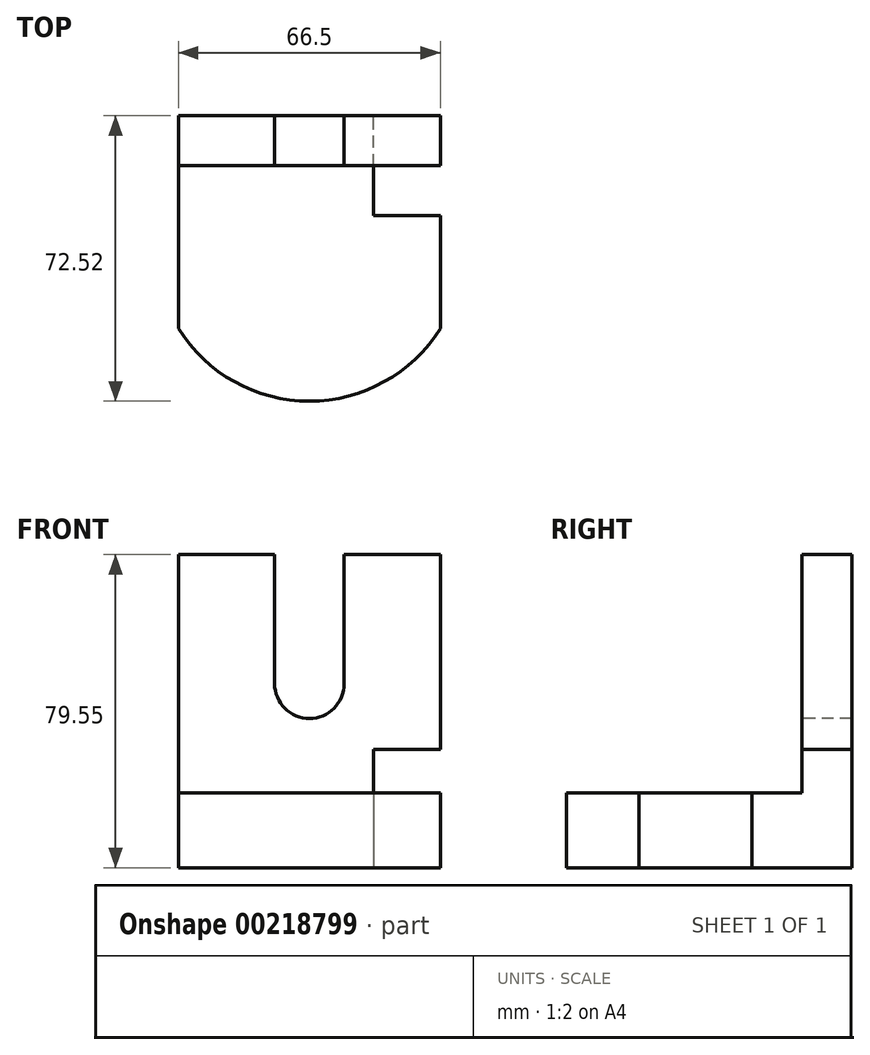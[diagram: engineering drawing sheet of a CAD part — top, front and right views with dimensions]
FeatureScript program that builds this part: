
annotation { "Feature Type Name" : "Feature", "Feature Type Description" : "" }
export const myFeature = defineFeature(function(context is Context, id is Id, definition is map)
    precondition{}
    {
        {
            var Q0;
            Q0=qCreatedBy(makeId("Top.planeOp"),FACE);
            var sketch = newSketch(context, id + "F0", { "sketchPlane" : qUnion([Q0])});
            skLineSegment(sketch, "E0.bottom", {"start": v(33.25, 20.67) * mm, "end": v(-33.25, 20.67) * mm});
            skLineSegment(sketch, "E0.left", {"start": v(33.25, 20.67) * mm, "end": v(33.25, -20.67) * mm});
            skLineSegment(sketch, "E0.right", {"start": v(-33.25, 20.67) * mm, "end": v(-33.25, -20.67) * mm});
            skPoint(sketch, "E0.middle", {"position": v(0, 0) * mm});
            skArc(sketch, "E1", {"start": v(-33.25, -20.67) * mm, "mid": v(0, -39.15) * mm, "end": v(33.25, -20.67) * mm});
            skSolve(sketch);
        }
        {
            var Q0;
            Q0=makeQuery(id+"F0.imprint","IMPRINT",FACE,{"disambiguationData":[TD([[makeQuery(id+"F0.imprint","IMPRINT",EDGE,{"derivedFrom":sQuery(id+"F0.wireOp",EDGE,"E0.bottom")}),1.0]])]});
            extrude(context, id + "F1", {"entities" : qUnion([Q0]), "depth" : 19.05 * mm});
        }
        {
            var Q0;
            Q0=makeQuery(id+"F1.opExtrude","SWEPT_FACE",FACE,{"disambiguationData":[OSD([sQuery(id+"F0.wireOp",EDGE,"E0.bottom")])]});
            var sketch = newSketch(context, id + "F2", { "sketchPlane" : qUnion([Q0])});
            skLineSegment(sketch, "E2.0.0", {"start": v(-33.25, 0) * mm, "end": v(33.25, 0) * mm});
            skLineSegment(sketch, "E2.0.1", {"start": v(33.25, 0) * mm, "end": v(33.25, 19.05) * mm});
            skLineSegment(sketch, "E2.0.3", {"start": v(-33.25, 19.05) * mm, "end": v(-33.25, 0) * mm});
            skLineSegment(sketch, "E3.bottom", {"start": v(33.25, 0) * mm, "end": v(-33.25, 0) * mm});
            skLineSegment(sketch, "E3.top", {"start": v(33.25, 79.55) * mm, "end": v(8.84, 79.55) * mm});
            skLineSegment(sketch, "E3.left", {"start": v(33.25, 0) * mm, "end": v(33.25, 79.55) * mm});
            skLineSegment(sketch, "E3.right", {"start": v(-33.25, 0) * mm, "end": v(-33.25, 79.55) * mm});
            skArc(sketch, "E4", {"start": v(-8.84, 46.78) * mm, "mid": v(0, 37.94) * mm, "end": v(8.84, 46.78) * mm});
            skLineSegment(sketch, "E5.top", {"start": v(-8.84, 79.55) * mm, "end": v(-15.81, 79.55) * mm});
            skLineSegment(sketch, "E5.left", {"start": v(8.84, 46.78) * mm, "end": v(8.84, 79.55) * mm});
            skLineSegment(sketch, "E6.right", {"start": v(-8.84, 79.55) * mm, "end": v(-8.84, 46.78) * mm});
            skLineSegment(sketch, "E7.trimOffspring", {"start": v(-15.81, 79.55) * mm, "end": v(-33.25, 79.55) * mm});
            skSolve(sketch);
        }
        {
            var Q0;
            Q0 = qSketchRegion(id + "F2", true);
            extrude(context, id + "F3", {"entities" : qUnion([Q0]), "operationType" : NewBodyOperationType.ADD, "depth" : 12.7 * mm});
        }
        {
            var Q0;
            Q0=makeQuery(id+"F3.opExtrude","CAP_FACE",FACE,{"disambiguationData":[OSD([sQuery(id+"F2.wireOp",EDGE,"E3.bottom"),sQuery(id+"F2.wireOp",EDGE,"E3.top"),sQuery(id+"F2.wireOp",EDGE,"E3.left"),sQuery(id+"F2.wireOp",EDGE,"E3.right"),sQuery(id+"F2.wireOp",EDGE,"E4"),sQuery(id+"F2.wireOp",EDGE,"E5.top"),sQuery(id+"F2.wireOp",EDGE,"E5.left"),sQuery(id+"F2.wireOp",EDGE,"E6.right"),sQuery(id+"F2.wireOp",EDGE,"E7.trimOffspring")])],"isStart":false});
            var sketch = newSketch(context, id + "F4", { "sketchPlane" : qUnion([Q0])});
            skLineSegment(sketch, "E8.bottom", {"start": v(-33.25, 30.1) * mm, "end": v(-16.28, 30.1) * mm});
            skLineSegment(sketch, "E8.top", {"start": v(-33.25, 0) * mm, "end": v(-16.28, 0) * mm});
            skLineSegment(sketch, "E8.left", {"start": v(-33.25, 30.1) * mm, "end": v(-33.25, 0) * mm});
            skLineSegment(sketch, "E8.right", {"start": v(-16.28, 30.1) * mm, "end": v(-16.28, 0) * mm});
            skSolve(sketch);
        }
        {
            var Q0;
            Q0=makeQuery(id+"F4.imprint","IMPRINT",FACE,{"disambiguationData":[TD([[makeQuery(id+"F4.imprint","IMPRINT",EDGE,{"derivedFrom":sQuery(id+"F4.wireOp",EDGE,"E8.bottom")}),-1.0]])]});
            extrude(context, id + "F5", {"entities" : qUnion([Q0]), "operationType" : NewBodyOperationType.REMOVE, "oppositeDirection" : true, "depth" : 25.4 * mm});
        }
    });
